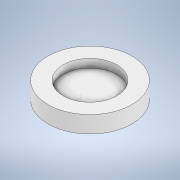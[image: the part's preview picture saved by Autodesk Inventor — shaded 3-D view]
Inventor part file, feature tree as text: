
AUTODESK INVENTOR PART (.ipt)
format: ipt  version: 2022 (Build 260153000, 153)  size: 166,400 bytes
history: native  units: mm
features: sketch x15, extrude x13
ambient origin geometry x8: Origin, YZ Plane, XZ Plane, XY Plane, X Axis, Y Axis, Z Axis, Center Point
bodies: Solid1 (feature_tree)
feature tree (28):
  sketch  "Sketch1"  dims[d0=50.0mm d1=10.0mm d2=0.0mm]
  sketch  "Sketch2"  dims[d3=32.0mm d4=5.0mm d5=0.0mm]
  extrude  "Extrusion1"  Depth=10.0mm TaperAngle=0.0deg
  extrude  "Extrusion2"  Depth=5.0mm TaperAngle=0.0deg
  sketch  "Sketch4"  dims[d9=5.0mm d10=2.0mm d11=0.0mm]
  extrude  "Extrusion3"  Depth=2.0mm TaperAngle=0.0deg
  extrude  "Extrusion4"  Depth=2.0mm TaperAngle=0.0deg
  extrude  "Extrusion5"  Depth=2.0mm TaperAngle=0.0deg
  extrude  "Extrusion6"  Depth=2.0mm TaperAngle=0.0deg
  extrude  "Extrusion7"  Depth=2.0mm TaperAngle=0.0deg
  extrude  "Extrusion8"  Depth=2.0mm TaperAngle=0.0deg
  extrude  "Extrusion9"  Depth=2.0mm TaperAngle=0.0deg
  extrude  "Extrusion10"  Depth=2.0mm TaperAngle=0.0deg
  extrude  "Extrusion11"  Depth=2.0mm TaperAngle=0.0deg
  extrude  "Extrusion12"  Depth=2.0mm TaperAngle=0.0deg
  extrude  "Extrusion13"  Depth=2.0mm TaperAngle=0.0deg
  sketch  "Sketch3"  dims[d6=5.0mm d7=2.0mm d8=0.0mm]
  sketch  "Sketch5"  dims[d12=5.0mm d13=2.0mm d14=0.0mm]
  sketch  "Sketch6"  dims[d15=5.0mm d16=2.0mm d17=0.0mm]
  sketch  "Sketch7"  dims[d18=5.0mm d19=2.0mm d20=0.0mm]
  sketch  "Sketch8"  dims[d21=5.0mm d22=2.0mm d23=0.0mm]
  sketch  "Sketch9"  dims[d24=5.0mm d25=2.0mm d26=0.0mm]
  sketch  "Sketch10"  dims[d27=5.0mm d28=2.0mm d29=0.0mm]
  sketch  "Sketch11"  dims[d30=5.0mm d31=2.0mm d32=0.0mm]
  sketch  "Sketch12"  dims[d33=5.0mm d34=2.0mm d35=0.0mm]
  sketch  "Sketch13"  dims[d36=5.0mm d37=2.0mm d38=0.0mm]
  sketch  "Sketch14"
  sketch  "Sketch15"
